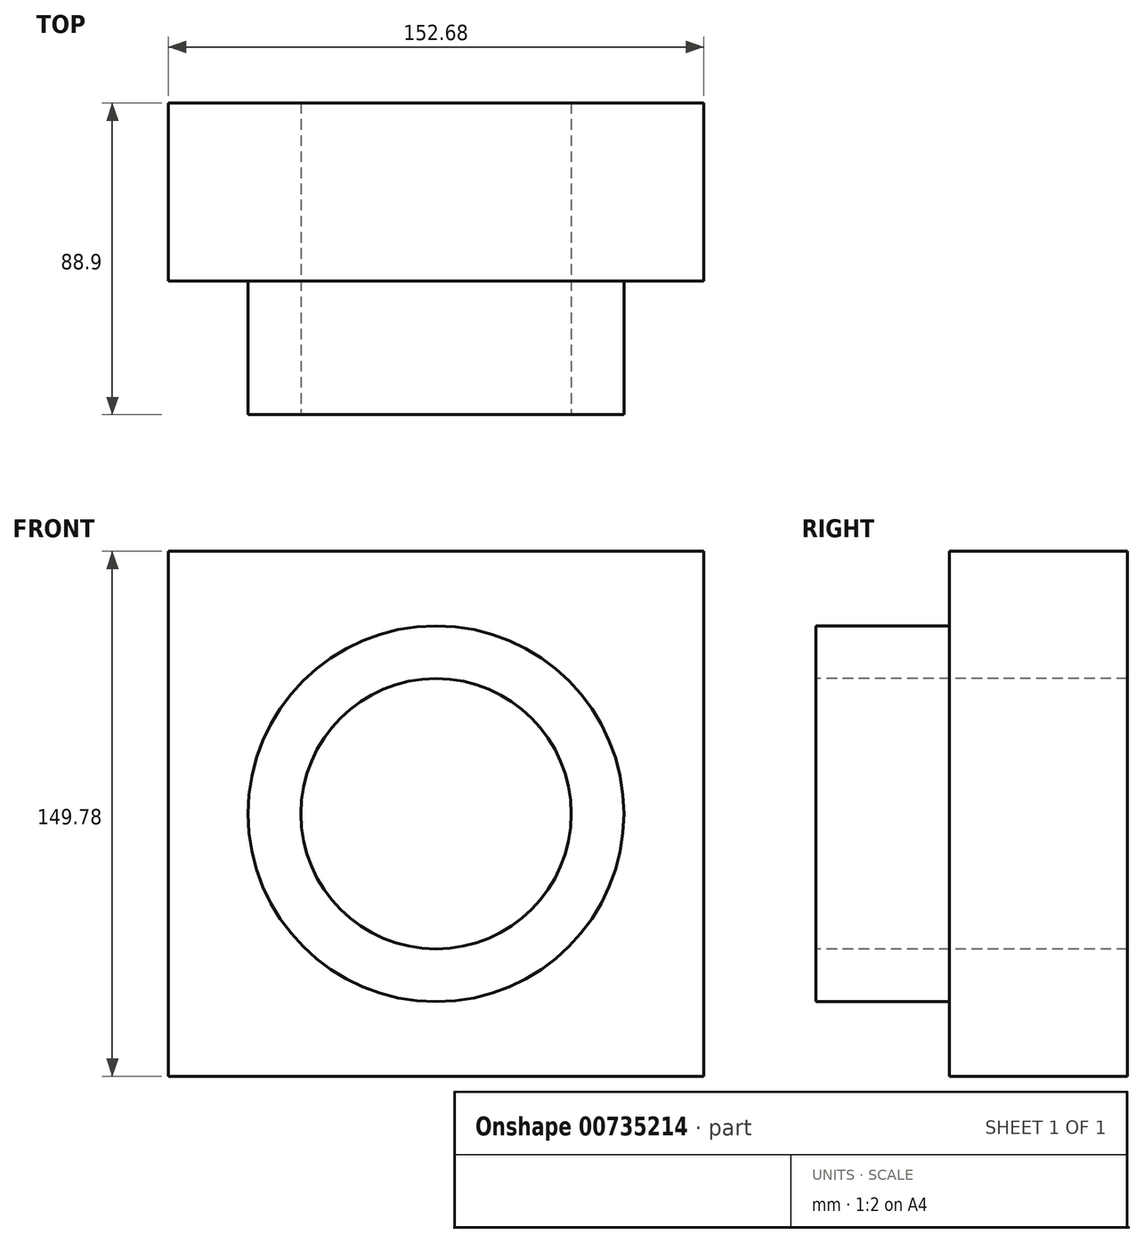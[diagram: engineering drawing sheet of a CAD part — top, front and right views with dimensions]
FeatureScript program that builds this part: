
annotation { "Feature Type Name" : "Feature", "Feature Type Description" : "" }
export const myFeature = defineFeature(function(context is Context, id is Id, definition is map)
    precondition{}
    {
        {
            var Q0;
            Q0=qCreatedBy(makeId("Front.planeOp"),FACE);
            var sketch = newSketch(context, id + "F0", { "sketchPlane" : qUnion([Q0])});
            skLineSegment(sketch, "E0.bottom", {"start": v(76.34, 74.9) * mm, "end": v(-76.34, 74.9) * mm});
            skLineSegment(sketch, "E0.top", {"start": v(76.34, -74.9) * mm, "end": v(-76.34, -74.9) * mm});
            skLineSegment(sketch, "E0.left", {"start": v(76.34, 74.9) * mm, "end": v(76.34, -74.9) * mm});
            skLineSegment(sketch, "E0.right", {"start": v(-76.34, 74.9) * mm, "end": v(-76.34, -74.9) * mm});
            skPoint(sketch, "E0.middle", {"position": v(0, 0) * mm});
            skSolve(sketch);
        }
        {
            var Q0;
            Q0=makeQuery(id+"F0.imprint","IMPRINT",FACE,{"disambiguationData":[TD([[makeQuery(id+"F0.imprint","IMPRINT",EDGE,{"derivedFrom":sQuery(id+"F0.wireOp",EDGE,"E0.bottom")}),1.0]])]});
            extrude(context, id + "F1", {"entities" : qUnion([Q0]), "depth" : 25.4 * mm, "offsetDistance" : 25.4 * mm, "hasSecondDirection" : true, "secondDirectionOppositeDirection" : true, "secondDirectionDepth" : 25.4 * mm});
        }
        {
            var Q0;
            Q0=makeQuery(id+"F1.opExtrude","CAP_FACE",FACE,{"disambiguationData":[OSD([sQuery(id+"F0.wireOp",EDGE,"E0.bottom"),sQuery(id+"F0.wireOp",EDGE,"E0.top"),sQuery(id+"F0.wireOp",EDGE,"E0.left"),sQuery(id+"F0.wireOp",EDGE,"E0.right")])],"isStart":false});
            var sketch = newSketch(context, id + "F2", { "sketchPlane" : qUnion([Q0])});
            skCircle(sketch, "E1", {"center": v(0, 0) * mm, "radius": 53.62 * mm});
            skSolve(sketch);
        }
        {
            var Q0;
            Q0 = qSketchRegion(id + "F2", true);
            extrude(context, id + "F3", {"entities" : qUnion([Q0]), "operationType" : NewBodyOperationType.ADD, "depth" : 38.1 * mm, "offsetDistance" : 25.4 * mm});
        }
        {
            var Q0;
            Q0=makeQuery(id+"F3.opExtrude","CAP_FACE",FACE,{"disambiguationData":[OSD([sQuery(id+"F2.wireOp",EDGE,"E1")])],"isStart":false});
            var sketch = newSketch(context, id + "F4", { "sketchPlane" : qUnion([Q0])});
            skCircle(sketch, "E2", {"center": v(0, 0) * mm, "radius": 38.57 * mm});
            skSolve(sketch);
        }
        {
            var Q0;
            Q0 = qSketchRegion(id + "F4", true);
            extrude(context, id + "F5", {"entities" : qUnion([Q0]), "operationType" : NewBodyOperationType.REMOVE, "oppositeDirection" : true, "depth" : 127 * mm, "offsetDistance" : 25.4 * mm});
        }
    });
